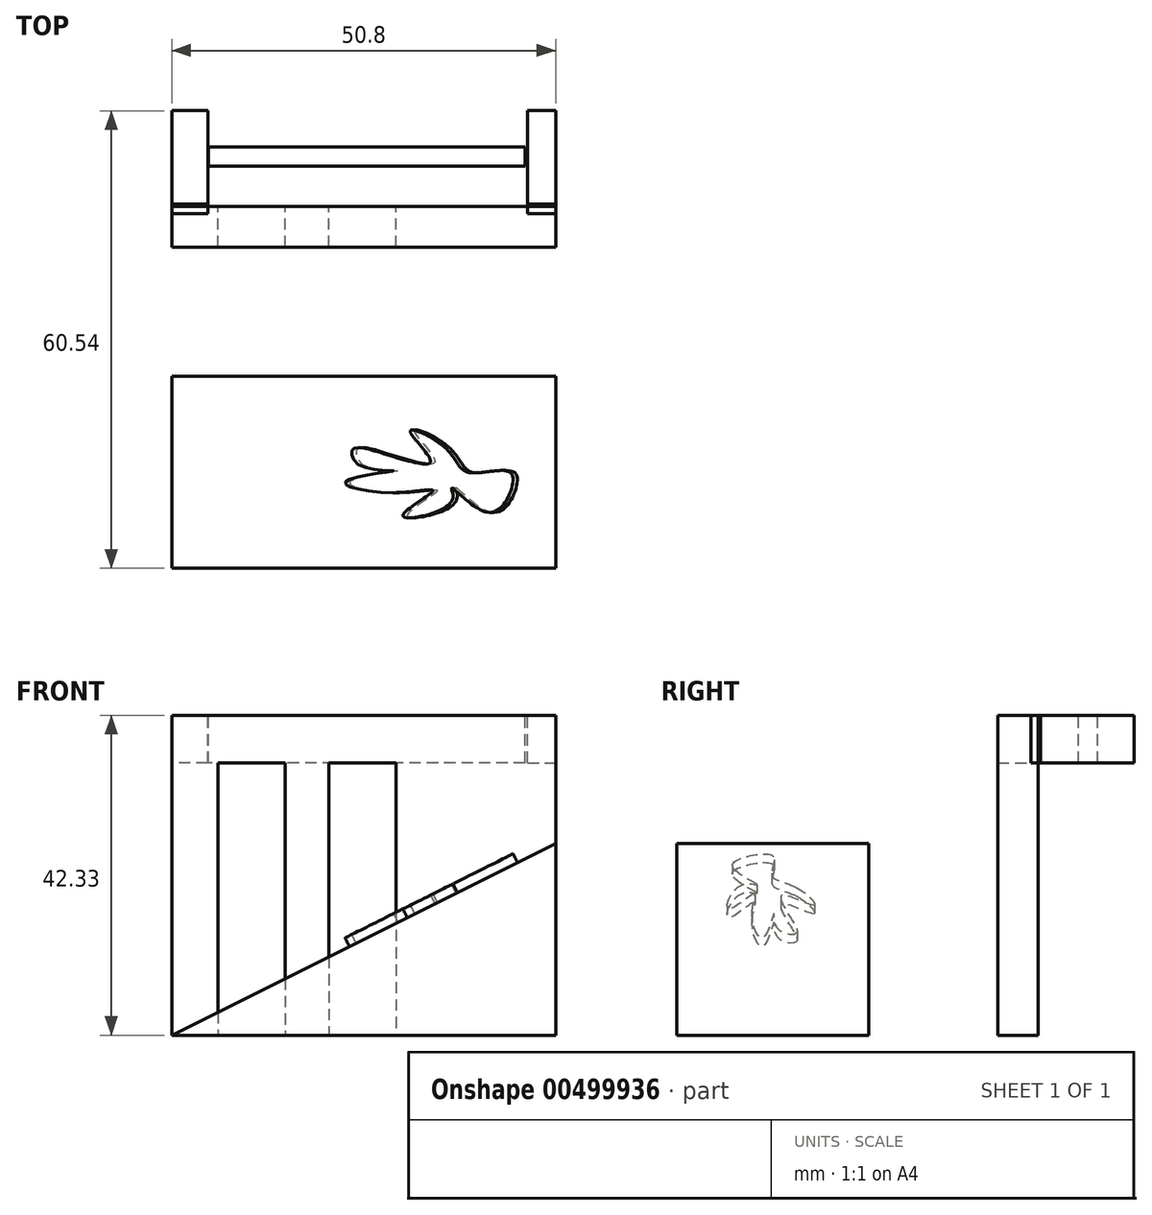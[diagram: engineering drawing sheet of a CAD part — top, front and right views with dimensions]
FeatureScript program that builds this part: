
annotation { "Feature Type Name" : "Feature", "Feature Type Description" : "" }
export const myFeature = defineFeature(function(context is Context, id is Id, definition is map)
    precondition{}
    {
        {
            var Q0;
            Q0=qCreatedBy(makeId("Front.planeOp"),FACE);
            var sketch = newSketch(context, id + "F0", { "sketchPlane" : qUnion([Q0])});
            skLineSegment(sketch, "E0", {"start": v(0, 0) * mm, "end": v(50.8, 0) * mm});
            skLineSegment(sketch, "E1", {"start": v(50.8, 0) * mm, "end": v(50.8, 25.4) * mm});
            skLineSegment(sketch, "E2", {"start": v(0, 0) * mm, "end": v(50.8, 25.4) * mm});
            skSolve(sketch);
        }
        {
            var Q0;
            Q0=makeQuery(id+"F0.imprint","IMPRINT",FACE,{"disambiguationData":[TD([[makeQuery(id+"F0.imprint","IMPRINT",EDGE,{"derivedFrom":sQuery(id+"F0.wireOp",EDGE,"E0")}),1.0]])]});
            extrude(context, id + "F1", {"entities" : qUnion([Q0]), "depth" : 25.4 * mm});
        }
        {
            var Q0;
            Q0=qCreatedBy(makeId("Right.planeOp"),FACE);
            var sketch = newSketch(context, id + "F2", { "sketchPlane" : qUnion([Q0])});
            skLineSegment(sketch, "E3", {"start": v(17.1, 0) * mm, "end": v(17.1, 42.33) * mm});
            skLineSegment(sketch, "E4", {"start": v(17.1, 42.33) * mm, "end": v(22.44, 42.33) * mm});
            skLineSegment(sketch, "E5", {"start": v(22.44, 42.33) * mm, "end": v(22.44, 0) * mm});
            skLineSegment(sketch, "E6", {"start": v(22.44, 0) * mm, "end": v(17.1, 0) * mm});
            skSolve(sketch);
        }
        {
            var Q0;
            Q0=makeQuery(id+"F2.imprint","IMPRINT",FACE,{"disambiguationData":[TD([[makeQuery(id+"F2.imprint","IMPRINT",EDGE,{"derivedFrom":sQuery(id+"F2.wireOp",EDGE,"E3")}),-1.0]])]});
            extrude(context, id + "F3", {"entities" : qUnion([Q0]), "depth" : 50.8 * mm});
        }
        {
            var Q0;
            Q0=makeQuery(id+"F3.opExtrude","SWEPT_FACE",FACE,{"disambiguationData":[OSD([sQuery(id+"F2.wireOp",EDGE,"E5")])]});
            var sketch = newSketch(context, id + "F4", { "sketchPlane" : qUnion([Q0])});
            skLineSegment(sketch, "E7.bottom", {"start": v(-6.11, 0) * mm, "end": v(-15, 0) * mm});
            skLineSegment(sketch, "E7.top", {"start": v(-8.49, 42.33) * mm, "end": v(-11.87, 42.33) * mm});
            skLineSegment(sketch, "E8.bottom", {"start": v(-20.78, 0) * mm, "end": v(-29.67, 0) * mm});
            skLineSegment(sketch, "E8.top", {"start": v(-23.2, 42.33) * mm, "end": v(-28.1, 42.33) * mm});
            skLineSegment(sketch, "E9.bottom", {"start": v(-35.13, 0) * mm, "end": v(-44.02, 0) * mm});
            skLineSegment(sketch, "E10.top", {"start": v(-35.13, 36.05) * mm, "end": v(-44.02, 36.05) * mm});
            skLineSegment(sketch, "E10.left", {"start": v(-35.13, 0) * mm, "end": v(-35.13, 36.05) * mm});
            skLineSegment(sketch, "E10.right", {"start": v(-44.02, 0) * mm, "end": v(-44.02, 36.05) * mm});
            skLineSegment(sketch, "E11.top", {"start": v(-20.78, 36.04) * mm, "end": v(-29.67, 36.04) * mm});
            skLineSegment(sketch, "E11.left", {"start": v(-20.78, 0) * mm, "end": v(-20.78, 36.04) * mm});
            skLineSegment(sketch, "E11.right", {"start": v(-29.67, 0) * mm, "end": v(-29.67, 36.04) * mm});
            skLineSegment(sketch, "E12.top", {"start": v(-6.11, 36.04) * mm, "end": v(-15, 36.04) * mm});
            skLineSegment(sketch, "E12.left", {"start": v(-6.11, 0) * mm, "end": v(-6.11, 36.04) * mm});
            skLineSegment(sketch, "E12.right", {"start": v(-15, 0) * mm, "end": v(-15, 36.04) * mm});
            skSolve(sketch);
        }
        {
            var Q0;
            Q0=makeQuery(id+"F4.imprint","IMPRINT",FACE,{"disambiguationData":[TD([[makeQuery(id+"F4.imprint","IMPRINT",EDGE,{"derivedFrom":sQuery(id+"F4.wireOp",EDGE,"E9.bottom")}),1.0]])]});
            var Q1;
            Q1=makeQuery(id+"F4.imprint","IMPRINT",FACE,{"disambiguationData":[TD([[makeQuery(id+"F4.imprint","IMPRINT",EDGE,{"derivedFrom":sQuery(id+"F4.wireOp",EDGE,"E8.bottom")}),1.0]])]});
            var Q2;
            Q2=makeQuery(id+"F4.imprint","IMPRINT",FACE,{"disambiguationData":[TD([[makeQuery(id+"F4.imprint","IMPRINT",EDGE,{"derivedFrom":sQuery(id+"F4.wireOp",EDGE,"E7.bottom")}),1.0]])]});
            extrude(context, id + "F5", {"entities" : qUnion([Q0, Q1, Q2]), "operationType" : NewBodyOperationType.REMOVE, "oppositeDirection" : true, "depth" : 6.35 * mm});
        }
        {
            var Q0;
            Q0=makeQuery(id+"F3.opExtrude","SWEPT_FACE",FACE,{"disambiguationData":[OSD([sQuery(id+"F2.wireOp",EDGE,"E5")])]});
            var sketch = newSketch(context, id + "F6", { "sketchPlane" : qUnion([Q0])});
            skLineSegment(sketch, "E13.bottom", {"start": v(0, 36.05) * mm, "end": v(-50.8, 36.05) * mm});
            skLineSegment(sketch, "E13.top", {"start": v(0, 42.33) * mm, "end": v(-50.8, 42.33) * mm});
            skLineSegment(sketch, "E13.left", {"start": v(0, 36.05) * mm, "end": v(0, 42.33) * mm});
            skLineSegment(sketch, "E13.right", {"start": v(-50.8, 36.05) * mm, "end": v(-50.8, 42.33) * mm});
            skSolve(sketch);
        }
        {
            var Q0;
            Q0=makeQuery(id+"F6.imprint","IMPRINT",FACE,{"disambiguationData":[TD([[makeQuery(id+"F6.imprint","IMPRINT",EDGE,{"derivedFrom":sQuery(id+"F6.wireOp",EDGE,"E13.top")}),-1.0]])]});
            extrude(context, id + "F7", {"entities" : qUnion([Q0]), "depth" : 12.7 * mm});
        }
        {
            var Q0;
            Q0=makeQuery(id+"F7.opExtrude","SWEPT_FACE",FACE,{"disambiguationData":[OSD([sQuery(id+"F6.wireOp",EDGE,"E13.top")])]});
            var sketch = newSketch(context, id + "F8", { "sketchPlane" : qUnion([Q0])});
            skLineSegment(sketch, "E14", {"start": v(46.75, 30.35) * mm, "end": v(4.88, 30.35) * mm});
            skLineSegment(sketch, "E15", {"start": v(4.88, 30.35) * mm, "end": v(4.88, 27.8) * mm});
            skLineSegment(sketch, "E16", {"start": v(4.88, 27.8) * mm, "end": v(46.75, 27.8) * mm});
            skLineSegment(sketch, "E17", {"start": v(46.75, 27.8) * mm, "end": v(46.75, 30.35) * mm});
            skSolve(sketch);
        }
        {
            var Q0;
            Q0=makeQuery(id+"F8.imprint","IMPRINT",FACE,{"disambiguationData":[TD([[makeQuery(id+"F8.imprint","IMPRINT",EDGE,{"derivedFrom":sQuery(id+"F8.wireOp",EDGE,"E14")}),-1.0]])]});
            var sketch = newSketch(context, id + "F9", { "sketchPlane" : qUnion([Q0])});
            skLineSegment(sketch, "E18.bottom", {"start": v(0, 22.8) * mm, "end": v(4.77, 22.8) * mm});
            skLineSegment(sketch, "E18.top", {"start": v(0, 35.35) * mm, "end": v(4.77, 35.35) * mm});
            skLineSegment(sketch, "E18.left", {"start": v(0, 22.8) * mm, "end": v(0, 35.35) * mm});
            skLineSegment(sketch, "E18.right", {"start": v(4.77, 22.8) * mm, "end": v(4.77, 35.35) * mm});
            skLineSegment(sketch, "E19.bottom", {"start": v(51.05, 22.8) * mm, "end": v(47.1, 22.8) * mm});
            skLineSegment(sketch, "E19.top", {"start": v(51.05, 35.35) * mm, "end": v(47.1, 35.35) * mm});
            skLineSegment(sketch, "E19.left", {"start": v(51.05, 22.8) * mm, "end": v(51.05, 35.35) * mm});
            skLineSegment(sketch, "E19.right", {"start": v(47.1, 22.8) * mm, "end": v(47.1, 35.35) * mm});
            skSolve(sketch);
        }
        {
            var Q0;
            {var subQ3=sQuery(id+"F9.wireOp",EDGE,"E18.bottom");Q0=makeQuery(id+"F9.imprint","IMPRINT",FACE,{"disambiguationData":[TD([[makeQuery(id+"F9.imprint","IMPRINT",EDGE,{"derivedFrom":subQ3}),-1.0]])]});}
            extrude(context, id + "F10", {"entities" : qUnion([Q0]), "operationType" : NewBodyOperationType.REMOVE, "oppositeDirection" : true, "depth" : 6.35 * mm});
        }
        {
            var Q0;
            Q0=makeQuery(id+"F10.boolean.opBoolean","COPY",FACE,{"derivedFrom":makeQuery(id+"F10.opExtrude","SWEPT_FACE",FACE,{"disambiguationData":[OSD([sQuery(id+"F9.wireOp",EDGE,"E18.bottom")])]})});
            extrude(context, id + "F11", {"entities" : qUnion([Q0]), "depth" : 1.27 * mm});
        }
        {
            var Q0;
            Q0=makeQuery(id+"F10.boolean.opBoolean","COPY",FACE,{"derivedFrom":makeQuery(id+"F10.opExtrude","SWEPT_FACE",FACE,{"disambiguationData":[OSD([sQuery(id+"F9.wireOp",EDGE,"E19.bottom")])]})});
            extrude(context, id + "F12", {"entities" : qUnion([Q0]), "depth" : 1.27 * mm});
        }
        {
            var Q0;
            Q0=makeQuery(id+"F1.opExtrude","SWEPT_FACE",FACE,{"disambiguationData":[OSD([sQuery(id+"F0.wireOp",EDGE,"E2")])]});
            var sketch = newSketch(context, id + "F13", { "sketchPlane" : qUnion([Q0])});
            skPoint(sketch, "E20.16.internal.snap0", {"position": v(50.63, -12.7) * mm});
            skFitSpline(sketch, "E20", {"points": [v(41.26, -9.62) * mm, v(35.93, -7.3) * mm, v(38.93, -11.21) * mm, v(31.82, -10.2) * mm, v(27.35, -9.76) * mm, v(28.58, -11.86) * mm, v(33.42, -12.52) * mm, v(26.4, -13.93) * mm, v(33.64, -15.4) * mm, v(39.2, -15.3) * mm, v(34.84, -18.47) * mm, v(42.04, -16.57) * mm, v(42.04, -14.76) * mm, v(47.1, -17.95) * mm, v(50.63, -15.57) * mm, v(50.63, -12.7) * mm, v(44.41, -12.7) * mm, v(41.26, -9.62) * mm]});
            skSolve(sketch);
        }
        {
            var Q0;
            Q0=makeQuery(id+"F1.opExtrude","SWEPT_FACE",FACE,{"disambiguationData":[OSD([sQuery(id+"F0.wireOp",EDGE,"E2")])]});
            var sketch = newSketch(context, id + "F14", { "sketchPlane" : qUnion([Q0])});
            skFitSpline(sketch, "E21", {"points": [v(28.9, -9.06) * mm, v(16.14, -3.81) * mm, v(22.93, -8.42) * mm, v(27.63, -11.07) * mm, v(28.9, -9.06) * mm]});
            skFitSpline(sketch, "E22", {"points": [v(26.67, -14.43) * mm, v(20.3, -15.82) * mm, v(16.14, -21.59) * mm, v(21.6, -18.85) * mm, v(26.67, -14.43) * mm]});
            skSolve(sketch);
        }
        {
            var Q0;
            Q0=makeQuery(id+"F13.imprint","IMPRINT",FACE,{"disambiguationData":[TD([[makeQuery(id+"F13.imprint","IMPRINT",EDGE,{"derivedFrom":sQuery(id+"F13.wireOp",EDGE,"E20")}),1.0]])]});
            extrude(context, id + "F15", {"entities" : qUnion([Q0]), "operationType" : NewBodyOperationType.ADD, "depth" : 1.27 * mm});
        }
        {
            var Q0;
            Q0=sQuery(id+"F14.wireOp",EDGE,"E22");
            var Q1;
            Q1=sQuery(id+"F14.wireOp",EDGE,"E21");
            extrude(context, id + "F16", {"bodyType" : ToolBodyType.SURFACE, "surfaceEntities" : qUnion([Q0, Q1]), "depth" : 1.27 * mm});
        }
    });
